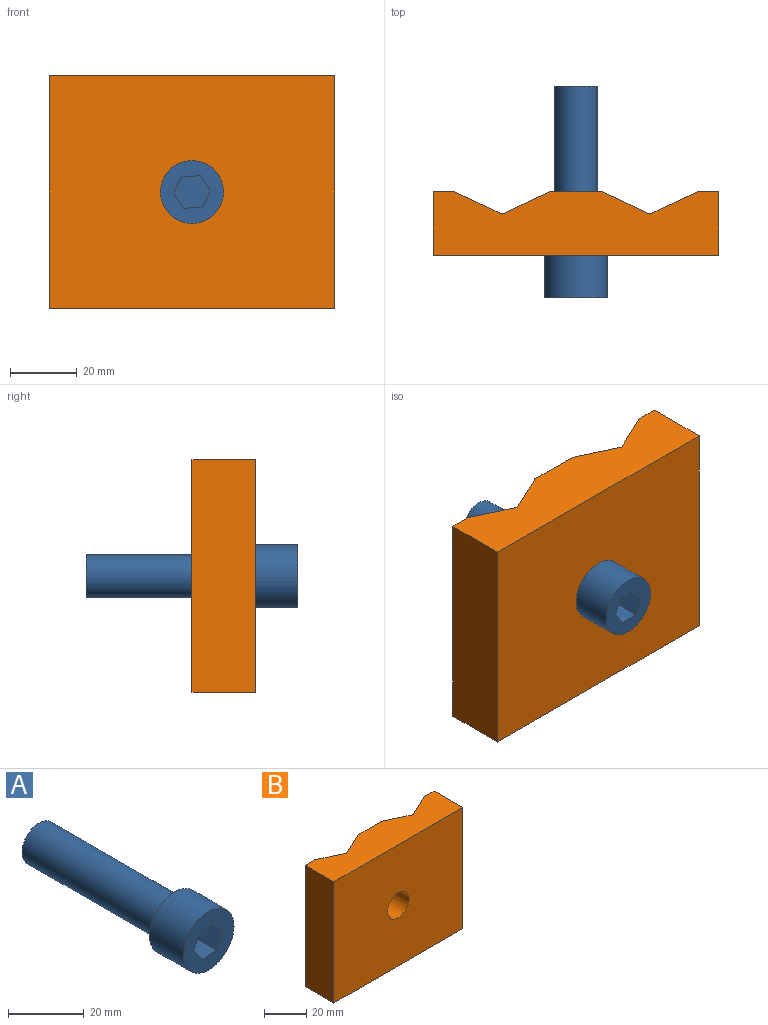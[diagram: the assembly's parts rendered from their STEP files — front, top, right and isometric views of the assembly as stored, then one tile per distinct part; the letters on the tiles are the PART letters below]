
ASSEMBLY  parts=2 mates=1
PART A: 12 faces, bbox 18.9x63.5x18.9 mm
  f0: plane 18.92x18.92mm, normal (0,1,0), area 154.6mm2, adj f3,f4
  f1: plane 12.7x12.7mm, normal (0,1,0), area 126.7mm2, adj f3
  f2: plane 9.53x5.49mm, normal (0.06,0,-1), area 52.4mm2, adj f6,f7,f9,f11
  f3: cylinder r=6.35mm len=50.8mm, axis (0,-1,0), area 2026.8mm2, adj f0,f1
  f4: cylinder r=9.46mm len=18.92mm, axis (0,-1,0), area 755mm2, adj f0,f7
  f5: plane 9.53x5.49mm, normal (-0.06,0,1), area 52.4mm2, adj f6,f7,f8,f10
  f6: plane 10.98x9.81mm, normal (0,-1,0), area 78.6mm2, adj f2,f5,f8,f9,f10,f11
  f7: plane 18.92x18.92mm, normal (0,-1,0), area 202.7mm2, adj f2,f4,f5,f8,f9,f10,f11
  f8: plane 9.53x4.6mm, normal (0.84,0,0.55), area 52.4mm2, adj f5,f6,f7,f9
  f9: plane 9.53x4.91mm, normal (0.89,0,-0.45), area 52.4mm2, adj f2,f6,f7,f8
  f10: plane 9.53x4.91mm, normal (-0.89,0,0.45), area 52.4mm2, adj f5,f6,f7,f11
  f11: plane 9.53x4.6mm, normal (-0.84,0,-0.55), area 52.4mm2, adj f2,f6,f7,f10
PART B: 13 faces, bbox 85.7x19.1x69.9 mm
  f0: cylinder r=7.14mm len=19.05mm, axis (0,-1,0), area 855.1mm2, adj f1,f2
  f1: plane 69.85x15.88mm, normal (0,1,0), area 948.5mm2, adj f0,f5,f7,f8,f12
  f2: plane 85.73x69.85mm, normal (0,-1,0), area 5827.6mm2, adj f0,f4,f5,f6,f12
  f3: plane 69.85x14.29mm, normal (0.42,0.91,0), area 1101.2mm2, adj f5,f7,f9,f12
  f4: plane 69.85x19.05mm, normal (1,0,0), area 1330.6mm2, adj f2,f5,f10,f12
  f5: plane 85.73x19.05mm, normal (0,0,-1), area 1442.7mm2, adj f1,f2,f3,f4,f6,f7,f8,f9
  f6: plane 69.85x19.05mm, normal (-1,0,0), area 1330.6mm2, adj f2,f5,f9,f12
  f7: plane 69.85x14.29mm, normal (-0.42,0.91,0), area 1101.2mm2, adj f1,f3,f5,f12
  f8: plane 69.85x14.29mm, normal (0.42,0.91,0), area 1101.2mm2, adj f1,f5,f11,f12
  f9: plane 69.85x6.35mm, normal (0,1,0), area 443.5mm2, adj f3,f5,f6,f12
  f10: plane 69.85x6.35mm, normal (0,1,0), area 443.5mm2, adj f4,f5,f11,f12
  f11: plane 69.85x14.29mm, normal (-0.42,0.91,0), area 1101.2mm2, adj f5,f8,f10,f12
  f12: plane 85.73x19.05mm, normal (0,0,1), area 1442.7mm2, adj f1,f2,f3,f4,f6,f7,f8,f9
PLACE A t=(254,0.01,0)mm
PLACE B t=(165.1,0.01,0)mm
MATE fastened A.f3 <-> B.f0  axis (0,1,0) through (76.2,-68.68,0)mm
